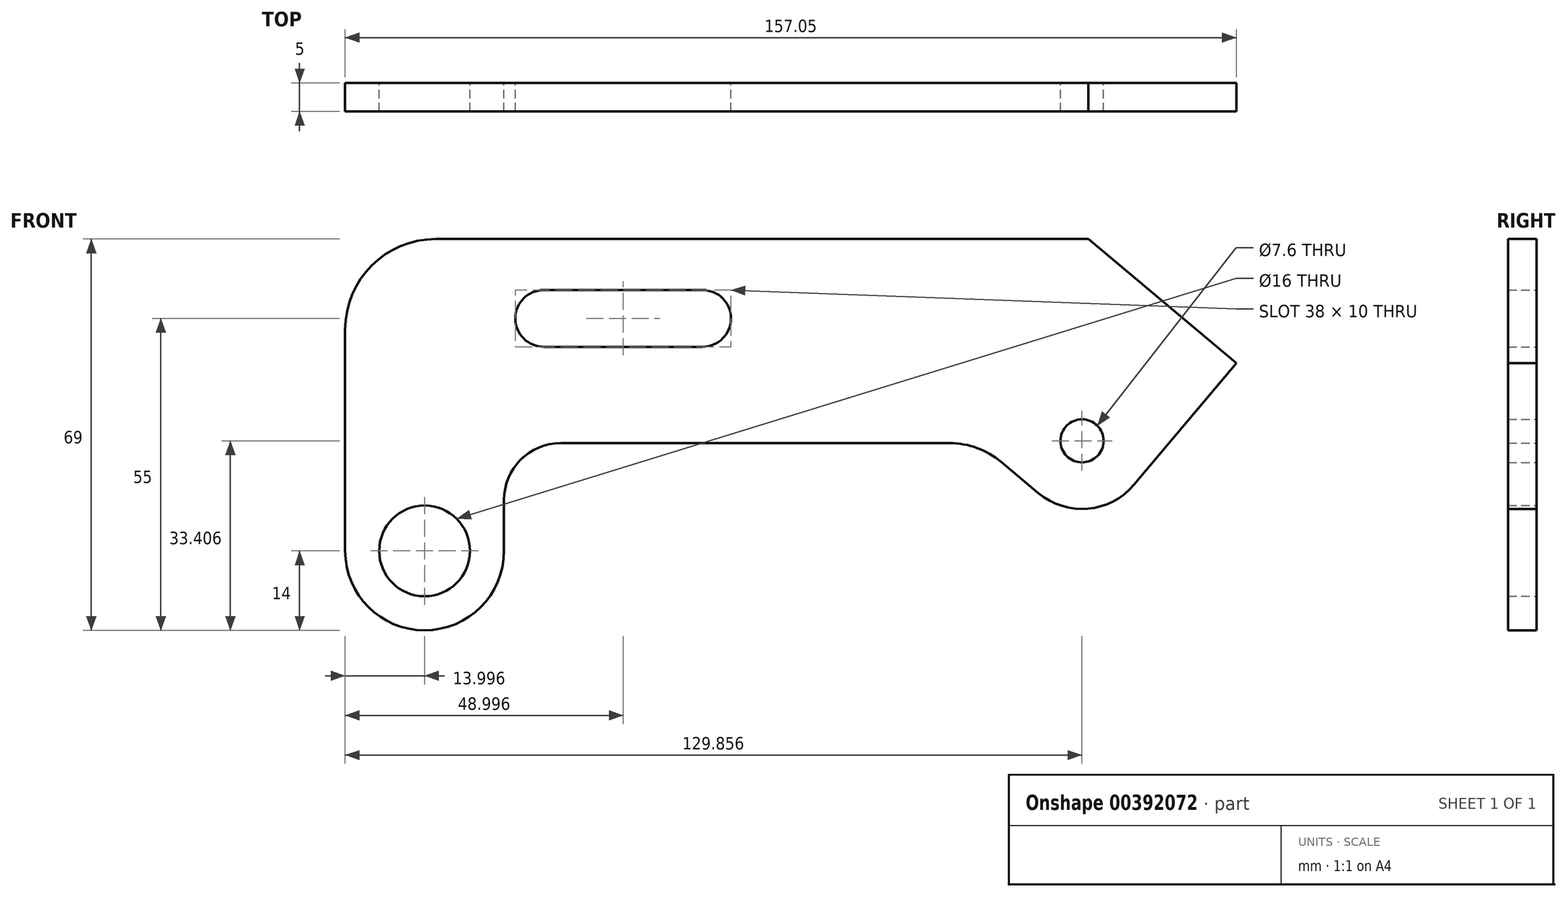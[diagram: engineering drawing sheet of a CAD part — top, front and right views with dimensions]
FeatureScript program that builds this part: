
annotation { "Feature Type Name" : "Feature", "Feature Type Description" : "" }
export const myFeature = defineFeature(function(context is Context, id is Id, definition is map)
    precondition{}
    {
        {
            var Q0;
            Q0=qCreatedBy(makeId("Front.planeOp"),FACE);
            var sketch = newSketch(context, id + "F0", { "sketchPlane" : qUnion([Q0])});
            skLineSegment(sketch, "E0", {"start": v(-92.94, 55) * mm, "end": v(38.06, 55) * mm});
            skLineSegment(sketch, "E1", {"start": v(38.06, 55) * mm, "end": v(64.1, 33.14) * mm});
            skLineSegment(sketch, "E2", {"start": v(64.1, 33.14) * mm, "end": v(46.1, 11.7) * mm});
            skLineSegment(sketch, "E3", {"start": v(29.2, 10.21) * mm, "end": v(18.73, 19) * mm});
            skLineSegment(sketch, "E4", {"start": v(18.73, 19) * mm, "end": v(-64.94, 19) * mm});
            skLineSegment(sketch, "E5", {"start": v(-64.94, 19) * mm, "end": v(-64.94, 0) * mm});
            skLineSegment(sketch, "E6", {"start": v(-64.94, 0) * mm, "end": v(-92.94, 0) * mm, "construction": true});
            skLineSegment(sketch, "E7", {"start": v(-92.94, 0) * mm, "end": v(-92.94, 55) * mm});
            skPoint(sketch, "E8.startSnap0", {"position": v(-78.94, 0) * mm});
            skPoint(sketch, "E9.orphan", {"position": v(-78.94, -14) * mm});
            skArc(sketch, "E10.converted", {"start": v(-92.94, 0) * mm, "mid": v(-78.94, -14) * mm, "end": v(-64.94, 0) * mm});
            skCircle(sketch, "E11", {"center": v(-78.94, 0) * mm, "radius": 8 * mm});
            skCircle(sketch, "E12", {"center": v(36.92, 19.4) * mm, "radius": 3.8 * mm});
            skArc(sketch, "E13", {"start": v(-57.94, 46) * mm, "mid": v(-62.94, 41) * mm, "end": v(-57.94, 36) * mm});
            skArc(sketch, "E14", {"start": v(-29.94, 36) * mm, "mid": v(-24.94, 41) * mm, "end": v(-29.94, 46) * mm});
            skLineSegment(sketch, "E15", {"start": v(-57.94, 46) * mm, "end": v(-29.94, 46) * mm});
            skLineSegment(sketch, "E16", {"start": v(-57.94, 36) * mm, "end": v(-29.94, 36) * mm});
            skPoint(sketch, "E17.visualSharp", {"position": v(38.4, 2.5) * mm});
            skArc(sketch, "E17.filletArc", {"start": v(29.2, 10.21) * mm, "mid": v(37.96, 7.45) * mm, "end": v(46.1, 11.7) * mm});
            skLineSegment(sketch, "E18", {"start": v(-78.94, 0) * mm, "end": v(-78.94, -36.88) * mm, "construction": true});
            skSolve(sketch);
        }
        {
            var Q0;
            Q0 = qSketchRegion(id + "F0", true);
            extrude(context, id + "F1", {"entities" : qUnion([Q0]), "depth" : 5 * mm});
        }
        {
            var Q0;
            Q0=makeQuery(id+"F1.opExtrude","SWEPT_EDGE",EDGE,{"disambiguationData":[OSD([sQuery(id+"F0.wireOp",EDGE,"E4"),sQuery(id+"F0.wireOp",EDGE,"E5")])]});
            fillet(context, id + "F2", {"entities" : qUnion([Q0]), "radius" : 10 * mm, "tangentPropagation" : true, "allowEdgeOverflow" : false});
        }
        {
            var Q0;
            Q0=makeQuery(id+"F1.opExtrude","SWEPT_EDGE",EDGE,{"disambiguationData":[OSD([sQuery(id+"F0.wireOp",EDGE,"E3"),sQuery(id+"F0.wireOp",EDGE,"E4")])]});
            fillet(context, id + "F3", {"entities" : qUnion([Q0]), "radius" : 14 * mm, "tangentPropagation" : true, "allowEdgeOverflow" : false});
        }
        {
            var Q0;
            Q0=makeQuery(id+"F1.opExtrude","SWEPT_EDGE",EDGE,{"disambiguationData":[OSD([sQuery(id+"F0.wireOp",EDGE,"E0"),sQuery(id+"F0.wireOp",EDGE,"E7")])]});
            fillet(context, id + "F4", {"entities" : qUnion([Q0]), "radius" : 16 * mm, "tangentPropagation" : true, "allowEdgeOverflow" : false});
        }
    });
